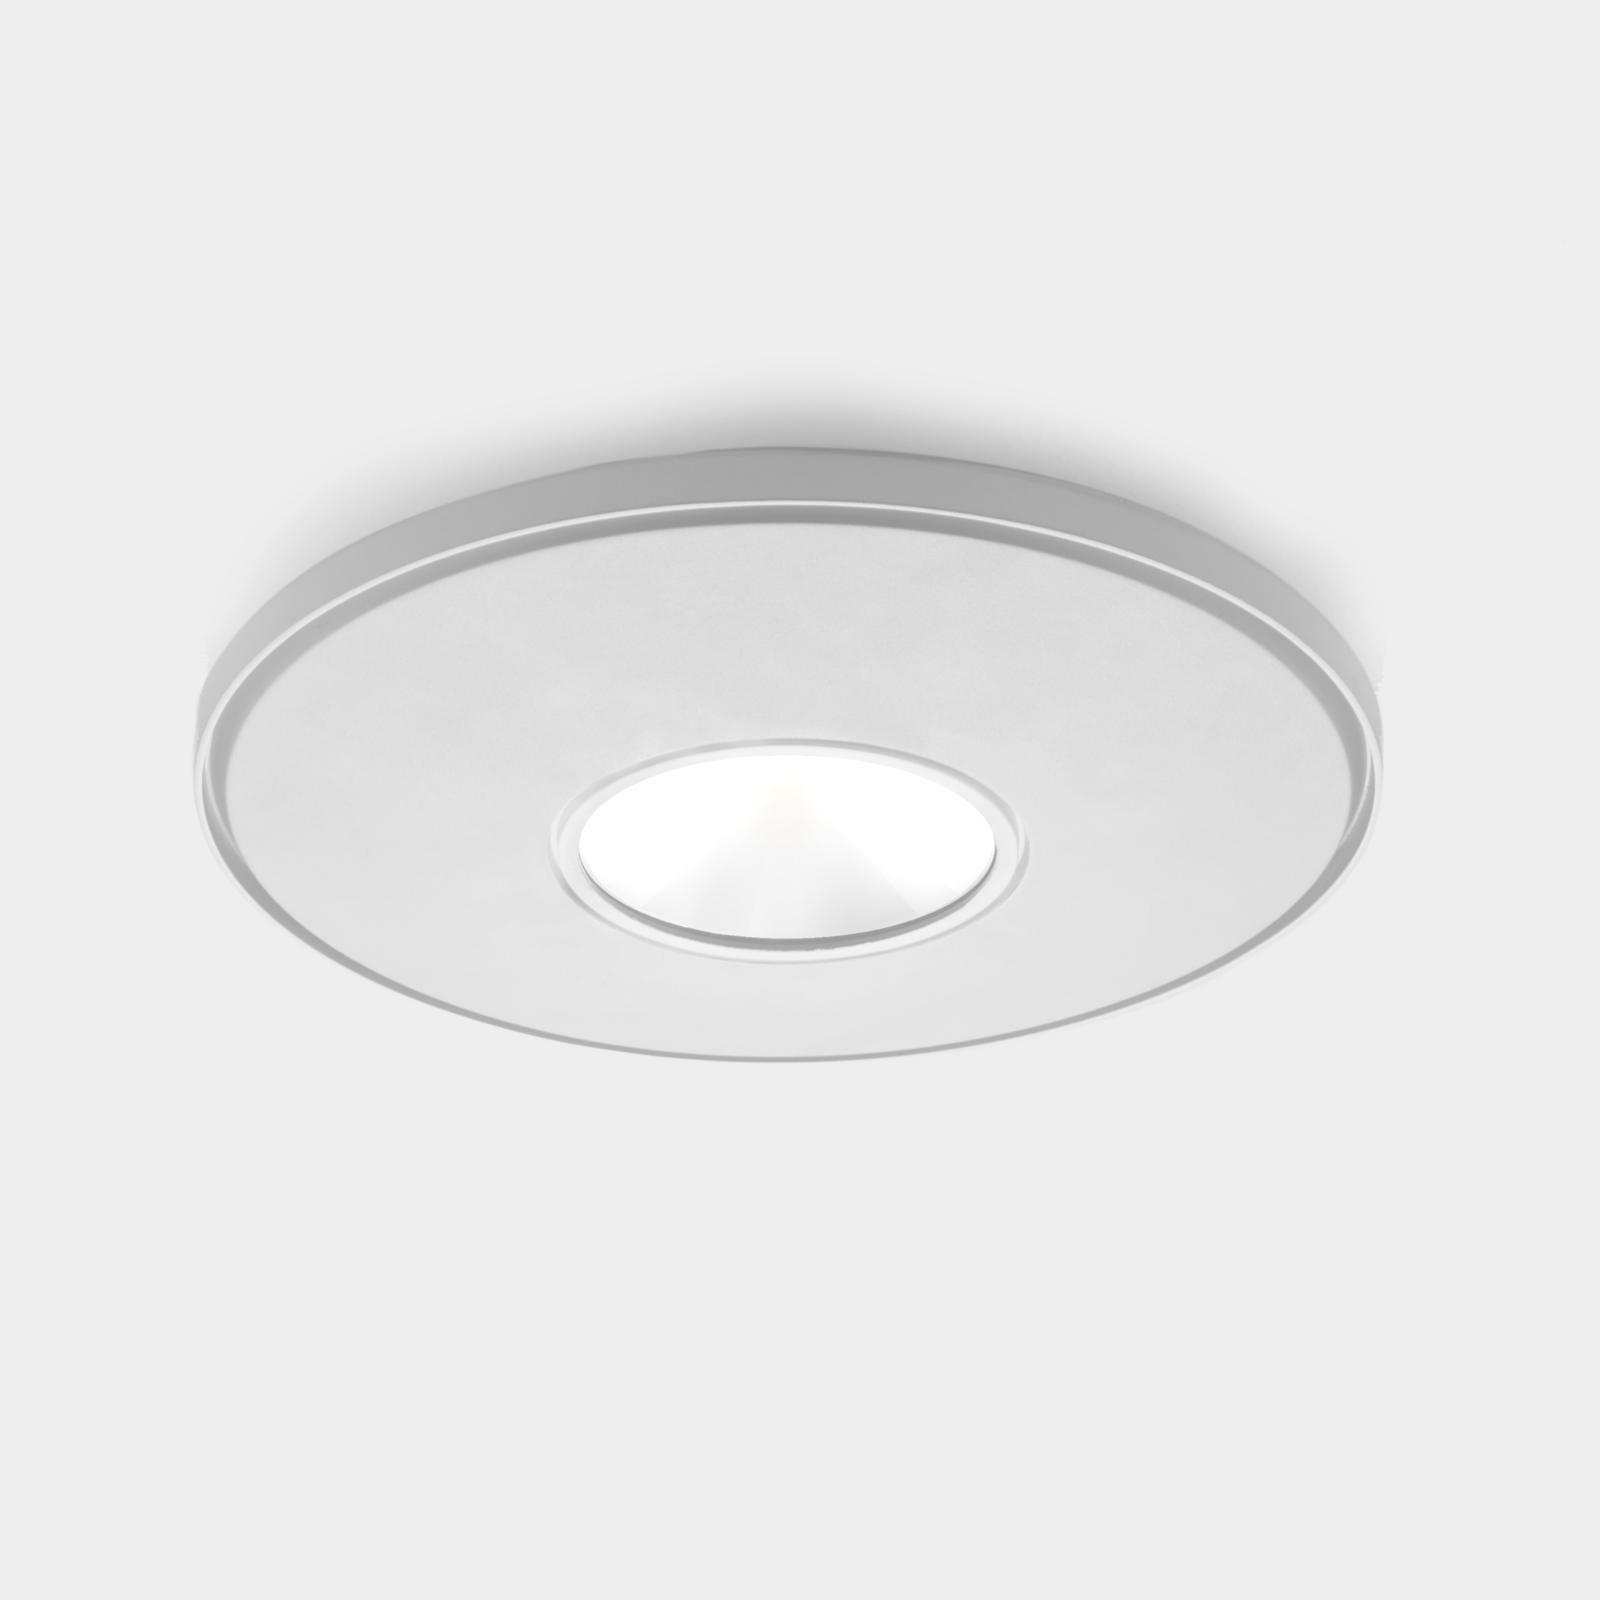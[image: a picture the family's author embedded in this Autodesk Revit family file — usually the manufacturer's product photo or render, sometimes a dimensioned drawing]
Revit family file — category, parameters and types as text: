
# Revit family: PF 30
name_source: partatom
category: Lighting Fixtures
units: mm (PartAtom-declared; Revit-internal decimal feet)

## family parameters
Cut with Voids When Loaded = No
Host = Face
Light Source = Yes
OmniClass Number = 23.80.70.11
OmniClass Title = Luminaries for Internal Lighting
Part Type = Normal
Room Calculation Point = No
Round Connector Dimension = Use Diameter
Shared = No

## types (2) — shared parameters
Beam angle (°) = 100°
CRI L'indice di Resa Cromatica = 85
Color Filter = 16777215
Description = Plafoniera dallo spessore estremamente ridotto, progettata appositamente per le nuove sorgenti a LED COB ad alta intensità luminosa ed elevato rendimento.
Il particolare design del retro è stato studiato per rispondere all'esigenza tecnica di dissipare passivamente il calore emesso dalla fonte luminosa. Esile e discreta, PF 30 si inserisce con semplicità in qualsiasi contesto pubblico e privato. Lo spessore, ridotto al minimo, consente all'apparecchio di integrarsi lungo le superfici.
Dimming Lamp Color Temperature Shift = <None>
Effective Intensity (lm) = 2448
Glass material = Glass
Lamp = LED 3400lm 26W 3000K CRI85
Larghezza = 300 mm
Manufacturer = ARIA
Photometric Web File = 3888-02 _ PF 30 LED 26W 3400 lm diff-1.IES
Tilt Angle = 90.00°
Type Comments = Ceiling / Wall light
URL = https://www.aria.lighting
Wattage Comments = 26

## per-type parameters (varying)
| type | Body material | Codice | Model | Type Image |
| PF 30 3400lm 26W 3000K CRI85-100°- WHITE | White Powder Coated Aluminium | 3888-02-21 | 3888-02-21 | PF 30 ARIA WHITE.jpg |
| PF 30 3400lm 26W 3000K CRI85-100°- METAL | Aluminum | 3888-02-52 | 3888-02-52 | PF 30 ARIA METAL.jpg |

## geometry (parser evidence)
native form markers: Sweep x3
no freeform markers — native parametric forms only
